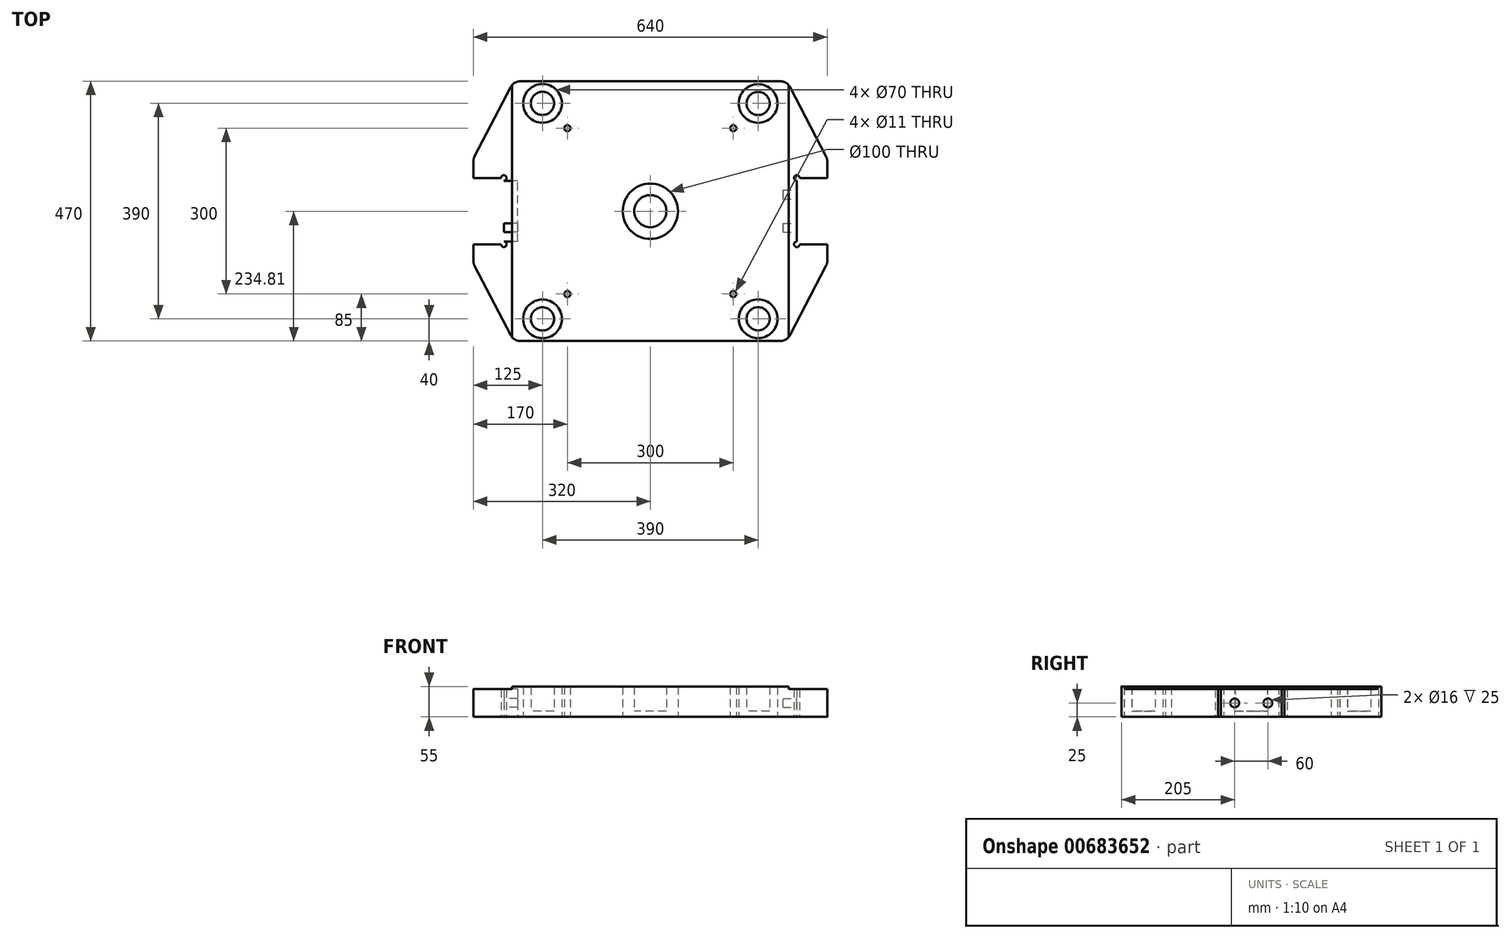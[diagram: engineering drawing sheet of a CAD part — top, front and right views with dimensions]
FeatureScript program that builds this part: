
annotation { "Feature Type Name" : "Feature", "Feature Type Description" : "" }
export const myFeature = defineFeature(function(context is Context, id is Id, definition is map)
    precondition{}
    {
        {
            var Q0;
            Q0=qCreatedBy(makeId("Top.planeOp"),FACE);
            var sketch = newSketch(context, id + "F0", { "sketchPlane" : qUnion([Q0])});
            skLineSegment(sketch, "E0", {"start": v(-270, -60) * mm, "end": v(-320, -60) * mm});
            skArc(sketch, "E1", {"start": v(-270, -60) * mm, "mid": v(-261.46, -63.54) * mm, "end": v(-265, -55) * mm});
            skLineSegment(sketch, "E2", {"start": v(-265, -55) * mm, "end": v(-265, 55) * mm});
            skArc(sketch, "E3", {"start": v(-265, 55) * mm, "mid": v(-261.46, 63.54) * mm, "end": v(-270, 60) * mm});
            skLineSegment(sketch, "E4", {"start": v(-270, 60) * mm, "end": v(-320, 60) * mm});
            skLineSegment(sketch, "E5", {"start": v(270, 60) * mm, "end": v(320, 60) * mm});
            skArc(sketch, "E6", {"start": v(270, 60) * mm, "mid": v(261.46, 63.54) * mm, "end": v(265, 55) * mm});
            skLineSegment(sketch, "E7", {"start": v(265, -55) * mm, "end": v(265, 55) * mm});
            skArc(sketch, "E8", {"start": v(265, -55) * mm, "mid": v(261.46, -63.54) * mm, "end": v(270, -60) * mm});
            skLineSegment(sketch, "E9", {"start": v(270, -60) * mm, "end": v(320, -60) * mm});
            skCircle(sketch, "E10", {"center": v(0, 0) * mm, "radius": 29 * mm});
            skCircle(sketch, "E11", {"center": v(0, -0.19) * mm, "radius": 50 * mm});
            skArc(sketch, "E12", {"start": v(317.74, -99.23) * mm, "mid": v(319.43, -94.75) * mm, "end": v(320, -90) * mm});
            skArc(sketch, "E13", {"start": v(235, -235) * mm, "mid": v(245.38, -232.1) * mm, "end": v(252.74, -224.23) * mm});
            skLineSegment(sketch, "E14", {"start": v(235, -235) * mm, "end": v(-235, -235) * mm});
            skArc(sketch, "E15", {"start": v(-252.74, -224.23) * mm, "mid": v(-245.38, -232.1) * mm, "end": v(-235, -235) * mm});
            skCircle(sketch, "E16", {"center": v(150, -150) * mm, "radius": 5.5 * mm});
            skCircle(sketch, "E17", {"center": v(-150, -150) * mm, "radius": 5.5 * mm});
            skCircle(sketch, "E18", {"center": v(-195, -195) * mm, "radius": 21 * mm});
            skCircle(sketch, "E19", {"center": v(-195, -195) * mm, "radius": 35 * mm});
            skCircle(sketch, "E20", {"center": v(195, -194.81) * mm, "radius": 21 * mm});
            skCircle(sketch, "E21", {"center": v(195, -194.81) * mm, "radius": 35 * mm});
            skLineSegment(sketch, "E22", {"start": v(-252.74, -224.23) * mm, "end": v(-317.74, -99.23) * mm});
            skArc(sketch, "E23", {"start": v(-320, -90) * mm, "mid": v(-319.43, -94.75) * mm, "end": v(-317.74, -99.23) * mm});
            skLineSegment(sketch, "E24", {"start": v(252.74, -224.23) * mm, "end": v(317.74, -99.23) * mm});
            skLineSegment(sketch, "E25", {"start": v(-320, -60) * mm, "end": v(-320, -90) * mm});
            skLineSegment(sketch, "E26", {"start": v(320, -90) * mm, "end": v(320, -60) * mm});
            skLineSegment(sketch, "E27", {"start": v(235, 235) * mm, "end": v(-235, 235) * mm});
            skLineSegment(sketch, "E28", {"start": v(-320, 60) * mm, "end": v(-320, 90) * mm});
            skArc(sketch, "E29", {"start": v(-317.74, 99.23) * mm, "mid": v(-319.43, 94.75) * mm, "end": v(-320, 90) * mm});
            skCircle(sketch, "E30", {"center": v(-150, 150) * mm, "radius": 5.5 * mm});
            skCircle(sketch, "E31", {"center": v(150, 150) * mm, "radius": 5.5 * mm});
            skCircle(sketch, "E32", {"center": v(195, 194.81) * mm, "radius": 21 * mm});
            skCircle(sketch, "E33", {"center": v(195, 194.81) * mm, "radius": 35 * mm});
            skCircle(sketch, "E34", {"center": v(-195, 195) * mm, "radius": 21 * mm});
            skCircle(sketch, "E35", {"center": v(-195, 195) * mm, "radius": 35 * mm});
            skLineSegment(sketch, "E36", {"start": v(-252.74, 224.23) * mm, "end": v(-317.74, 99.23) * mm});
            skArc(sketch, "E37", {"start": v(-235, 235) * mm, "mid": v(-245.38, 232.1) * mm, "end": v(-252.74, 224.23) * mm});
            skArc(sketch, "E38", {"start": v(252.74, 224.23) * mm, "mid": v(245.38, 232.1) * mm, "end": v(235, 235) * mm});
            skLineSegment(sketch, "E39", {"start": v(252.74, 224.23) * mm, "end": v(317.74, 99.23) * mm});
            skArc(sketch, "E40", {"start": v(320, 90) * mm, "mid": v(319.43, 94.75) * mm, "end": v(317.74, 99.23) * mm});
            skLineSegment(sketch, "E41", {"start": v(320, 60) * mm, "end": v(320, 90) * mm});
            skSolve(sketch);
        }
        {
            var Q0;
            Q0=makeQuery(id+"F0.imprint","IMPRINT",FACE,{"disambiguationData":[TD([[makeQuery(id+"F0.imprint","IMPRINT",EDGE,{"derivedFrom":sQuery(id+"F0.wireOp",EDGE,"E34")}),1.0]])]});
            var Q1;
            Q1=makeQuery(id+"F0.imprint","IMPRINT",FACE,{"disambiguationData":[TD([[makeQuery(id+"F0.imprint","IMPRINT",EDGE,{"derivedFrom":sQuery(id+"F0.wireOp",EDGE,"E32")}),1.0]])]});
            var Q2;
            Q2=makeQuery(id+"F0.imprint","IMPRINT",FACE,{"disambiguationData":[TD([[makeQuery(id+"F0.imprint","IMPRINT",EDGE,{"derivedFrom":sQuery(id+"F0.wireOp",EDGE,"E0")}),1.0]])]});
            var Q3;
            Q3=makeQuery(id+"F0.imprint","IMPRINT",FACE,{"disambiguationData":[TD([[makeQuery(id+"F0.imprint","IMPRINT",EDGE,{"derivedFrom":sQuery(id+"F0.wireOp",EDGE,"E18")}),1.0]])]});
            var Q4;
            Q4=makeQuery(id+"F0.imprint","IMPRINT",FACE,{"disambiguationData":[TD([[makeQuery(id+"F0.imprint","IMPRINT",EDGE,{"derivedFrom":sQuery(id+"F0.wireOp",EDGE,"E10")}),1.0]])]});
            var Q5;
            Q5=makeQuery(id+"F0.imprint","IMPRINT",FACE,{"disambiguationData":[TD([[makeQuery(id+"F0.imprint","IMPRINT",EDGE,{"derivedFrom":sQuery(id+"F0.wireOp",EDGE,"E20")}),1.0]])]});
            extrude(context, id + "F1", {"entities" : qUnion([Q0, Q1, Q2, Q3, Q4, Q5]), "depth" : 55 * mm, "offsetDistance" : 25 * mm});
        }
        {
            var Q0;
            Q0=makeQuery(id+"F0.imprint","IMPRINT",FACE,{"disambiguationData":[TD([[makeQuery(id+"F0.imprint","IMPRINT",EDGE,{"derivedFrom":sQuery(id+"F0.wireOp",EDGE,"E32")}),1.0]])]});
            var Q1;
            Q1=makeQuery(id+"F0.imprint","IMPRINT",FACE,{"disambiguationData":[TD([[makeQuery(id+"F0.imprint","IMPRINT",EDGE,{"derivedFrom":sQuery(id+"F0.wireOp",EDGE,"E34")}),1.0]])]});
            var Q2;
            Q2=makeQuery(id+"F0.imprint","IMPRINT",FACE,{"disambiguationData":[TD([[makeQuery(id+"F0.imprint","IMPRINT",EDGE,{"derivedFrom":sQuery(id+"F0.wireOp",EDGE,"E10")}),1.0]])]});
            var Q3;
            Q3=makeQuery(id+"F0.imprint","IMPRINT",FACE,{"disambiguationData":[TD([[makeQuery(id+"F0.imprint","IMPRINT",EDGE,{"derivedFrom":sQuery(id+"F0.wireOp",EDGE,"E18")}),1.0]])]});
            var Q4;
            Q4=makeQuery(id+"F0.imprint","IMPRINT",FACE,{"disambiguationData":[TD([[makeQuery(id+"F0.imprint","IMPRINT",EDGE,{"derivedFrom":sQuery(id+"F0.wireOp",EDGE,"E20")}),1.0]])]});
            extrude(context, id + "F2", {"entities" : qUnion([Q0, Q1, Q2, Q3, Q4]), "operationType" : NewBodyOperationType.REMOVE, "depth" : 10 * mm, "offsetDistance" : 25 * mm});
        }
        {
            var Q0;
            Q0=makeQuery(id+"F1.opExtrude","CAP_FACE",FACE,{"disambiguationData":[OSD([sQuery(id+"F0.wireOp",EDGE,"E0"),sQuery(id+"F0.wireOp",EDGE,"E1"),sQuery(id+"F0.wireOp",EDGE,"E2"),sQuery(id+"F0.wireOp",EDGE,"E3"),sQuery(id+"F0.wireOp",EDGE,"E4"),sQuery(id+"F0.wireOp",EDGE,"E5"),sQuery(id+"F0.wireOp",EDGE,"E6"),sQuery(id+"F0.wireOp",EDGE,"E7"),sQuery(id+"F0.wireOp",EDGE,"E8"),sQuery(id+"F0.wireOp",EDGE,"E9"),sQuery(id+"F0.wireOp",EDGE,"E10"),sQuery(id+"F0.wireOp",EDGE,"E12"),sQuery(id+"F0.wireOp",EDGE,"E13"),sQuery(id+"F0.wireOp",EDGE,"E14"),sQuery(id+"F0.wireOp",EDGE,"E15"),sQuery(id+"F0.wireOp",EDGE,"E16"),sQuery(id+"F0.wireOp",EDGE,"E17"),sQuery(id+"F0.wireOp",EDGE,"E18"),sQuery(id+"F0.wireOp",EDGE,"E20"),sQuery(id+"F0.wireOp",EDGE,"E22"),sQuery(id+"F0.wireOp",EDGE,"E23"),sQuery(id+"F0.wireOp",EDGE,"E24"),sQuery(id+"F0.wireOp",EDGE,"E25"),sQuery(id+"F0.wireOp",EDGE,"E26"),sQuery(id+"F0.wireOp",EDGE,"E27"),sQuery(id+"F0.wireOp",EDGE,"E28"),sQuery(id+"F0.wireOp",EDGE,"E29"),sQuery(id+"F0.wireOp",EDGE,"E30"),sQuery(id+"F0.wireOp",EDGE,"E31"),sQuery(id+"F0.wireOp",EDGE,"E32"),sQuery(id+"F0.wireOp",EDGE,"E34"),sQuery(id+"F0.wireOp",EDGE,"E36"),sQuery(id+"F0.wireOp",EDGE,"E37"),sQuery(id+"F0.wireOp",EDGE,"E38"),sQuery(id+"F0.wireOp",EDGE,"E39"),sQuery(id+"F0.wireOp",EDGE,"E40"),sQuery(id+"F0.wireOp",EDGE,"E41")])],"isStart":false});
            var sketch = newSketch(context, id + "F3", { "sketchPlane" : qUnion([Q0])});
            skLineSegment(sketch, "E42.0", {"start": v(320, 60) * mm, "end": v(320, 90) * mm});
            skLineSegment(sketch, "E43.0", {"start": v(250, -265) * mm, "end": v(250, 285) * mm});
            skLineSegment(sketch, "E44", {"start": v(250, 285) * mm, "end": v(411.37, 285) * mm});
            skLineSegment(sketch, "E45", {"start": v(411.37, 285) * mm, "end": v(411.37, -265) * mm});
            skLineSegment(sketch, "E46", {"start": v(411.37, -265) * mm, "end": v(250, -265) * mm});
            skLineSegment(sketch, "E47.MirrorCS", {"start": v(-250, 285) * mm, "end": v(-411.37, 285) * mm});
            skLineSegment(sketch, "E48.MirrorCS", {"start": v(-250, -265) * mm, "end": v(-250, 285) * mm});
            skLineSegment(sketch, "E49.MirrorCS", {"start": v(-411.37, 285) * mm, "end": v(-411.37, -265) * mm});
            skLineSegment(sketch, "E50.MirrorCS", {"start": v(-411.37, -265) * mm, "end": v(-250, -265) * mm});
            skSolve(sketch);
        }
        {
            var Q0;
            Q0=makeQuery(id+"F3.imprint","IMPRINT",FACE,{"disambiguationData":[TD([[makeQuery(id+"F3.imprint","IMPRINT",EDGE,{"derivedFrom":sQuery(id+"F3.wireOp",EDGE,"E42.0")}),1.0]])]});
            var Q1;
            Q1=makeQuery(id+"F3.imprint","IMPRINT",FACE,{"disambiguationData":[TD([[makeQuery(id+"F3.imprint","IMPRINT",EDGE,{"derivedFrom":makeQuery(id+"F1.opExtrude","CAP_EDGE",EDGE,{"disambiguationData":[OSD([sQuery(id+"F0.wireOp",EDGE,"E0")])],"isStart":false})}),1.0]])]});
            extrude(context, id + "F4", {"entities" : qUnion([Q0, Q1]), "operationType" : NewBodyOperationType.REMOVE, "oppositeDirection" : true, "depth" : 5 * mm, "offsetDistance" : 25 * mm});
        }
        {
            var Q0;
            Q0=makeQuery(id+"F1.opExtrude","SWEPT_FACE",FACE,{"disambiguationData":[OSD([sQuery(id+"F0.wireOp",EDGE,"E7")])]});
            var sketch = newSketch(context, id + "F5", { "sketchPlane" : qUnion([Q0])});
            skLineSegment(sketch, "E51.0", {"start": v(49.81, 0) * mm, "end": v(-50.19, 0) * mm});
            skLineSegment(sketch, "E52.0", {"start": v(-55, 50) * mm, "end": v(55, 50) * mm});
            skCircle(sketch, "E53", {"center": v(30, 25) * mm, "radius": 8 * mm});
            skCircle(sketch, "E54", {"center": v(-30, 25) * mm, "radius": 8 * mm});
            skSolve(sketch);
        }
        {
            var Q0;
            Q0=makeQuery(id+"F5.imprint","IMPRINT",FACE,{"disambiguationData":[TD([[makeQuery(id+"F5.imprint","IMPRINT",EDGE,{"derivedFrom":sQuery(id+"F5.wireOp",EDGE,"E53")}),1.0]])]});
            var Q1;
            Q1=makeQuery(id+"F5.imprint","IMPRINT",FACE,{"disambiguationData":[TD([[makeQuery(id+"F5.imprint","IMPRINT",EDGE,{"derivedFrom":sQuery(id+"F5.wireOp",EDGE,"E54")}),1.0]])]});
            extrude(context, id + "F6", {"entities" : qUnion([Q0, Q1]), "operationType" : NewBodyOperationType.REMOVE, "oppositeDirection" : true, "depth" : 25 * mm, "offsetDistance" : 25 * mm});
        }
        {
            var Q0;
            Q0=makeQuery(id+"F1.opExtrude","SWEPT_FACE",FACE,{"disambiguationData":[OSD([sQuery(id+"F0.wireOp",EDGE,"E2")])]});
            var sketch = newSketch(context, id + "F7", { "sketchPlane" : qUnion([Q0])});
            skCircle(sketch, "E55", {"center": v(-30, 25) * mm, "radius": 8 * mm});
            skLineSegment(sketch, "E56", {"start": v(0, 0) * mm, "end": v(0, 50) * mm, "construction": true});
            skCircle(sketch, "E57.MirrorC", {"center": v(30, 25) * mm, "radius": 8 * mm});
            skSolve(sketch);
        }
        {
            var Q0;
            Q0=makeQuery(id+"F7.imprint","IMPRINT",FACE,{"disambiguationData":[TD([[makeQuery(id+"F7.imprint","IMPRINT",EDGE,{"derivedFrom":sQuery(id+"F7.wireOp",EDGE,"E55")}),1.0]])]});
            var Q1;
            Q1=makeQuery(id+"F7.imprint","IMPRINT",FACE,{"disambiguationData":[TD([[makeQuery(id+"F7.imprint","IMPRINT",EDGE,{"derivedFrom":sQuery(id+"F7.wireOp",EDGE,"E57.MirrorC")}),-1.0]])]});
            extrude(context, id + "F8", {"entities" : qUnion([Q0, Q1]), "operationType" : NewBodyOperationType.REMOVE, "oppositeDirection" : true, "depth" : 25 * mm, "offsetDistance" : 25 * mm});
        }
    });
